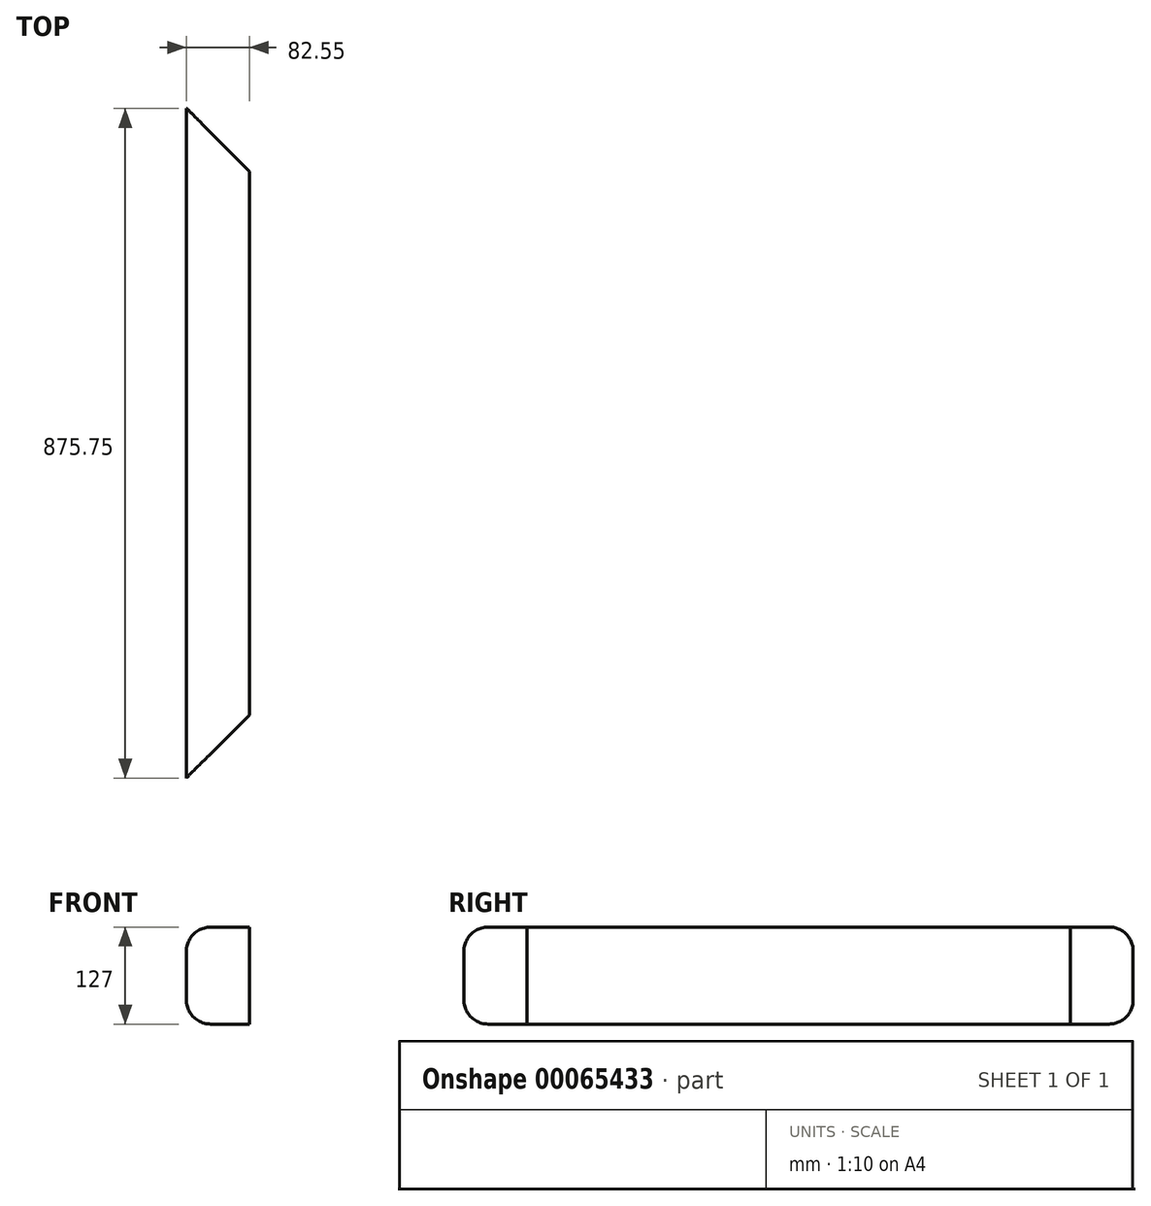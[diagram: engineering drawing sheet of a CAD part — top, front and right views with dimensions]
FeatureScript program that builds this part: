
annotation { "Feature Type Name" : "Feature", "Feature Type Description" : "" }
export const myFeature = defineFeature(function(context is Context, id is Id, definition is map)
    precondition{}
    {
        {
            var Q0;
            Q0=qCreatedBy(makeId("Front.planeOp"),FACE);
            var sketch = newSketch(context, id + "F0", { "sketchPlane" : qUnion([Q0])});
            skLineSegment(sketch, "E0.bottom", {"start": v(0, 0) * mm, "end": v(-50.8, 0) * mm});
            skLineSegment(sketch, "E0.top", {"start": v(0, -127) * mm, "end": v(-50.8, -127) * mm});
            skLineSegment(sketch, "E0.left", {"start": v(0, 0) * mm, "end": v(0, -127) * mm});
            skLineSegment(sketch, "E0.right", {"start": v(-82.55, -31.75) * mm, "end": v(-82.55, -95.25) * mm});
            skPoint(sketch, "E1.visualSharp", {"position": v(-82.55, 0) * mm});
            skArc(sketch, "E1.filletArc", {"start": v(-50.8, 0) * mm, "mid": v(-73.25, -9.3) * mm, "end": v(-82.55, -31.75) * mm});
            skPoint(sketch, "E2.visualSharp", {"position": v(-82.55, -127) * mm});
            skArc(sketch, "E2.filletArc", {"start": v(-82.55, -95.25) * mm, "mid": v(-73.25, -117.7) * mm, "end": v(-50.8, -127) * mm});
            skSolve(sketch);
        }
        {
            var Q0;
            Q0=qSketchRegion(id+"F0",true);
            extrude(context, id + "F1", {"entities" : qUnion([Q0]), "depth" : 1016 * mm});
        }
        {
            var Q0;
            Q0=makeQuery(id+"F1.opExtrude","SWEPT_FACE",FACE,{"disambiguationData":[OSD([sQuery(id+"F0.wireOp",EDGE,"E0.bottom")])]});
            var sketch = newSketch(context, id + "F2", { "sketchPlane" : qUnion([Q0])});
            skLineSegment(sketch, "E3", {"start": v(0, 0) * mm, "end": v(-82, 0) * mm});
            skLineSegment(sketch, "E4", {"start": v(-82, 0) * mm, "end": v(0, -82) * mm});
            skLineSegment(sketch, "E5", {"start": v(0, -82) * mm, "end": v(0, 0) * mm});
            skSolve(sketch);
        }
        {
            var Q0;
            Q0=qSketchRegion(id+"F2",true);
            extrude(context, id + "F3", {"entities" : qUnion([Q0]), "operationType" : NewBodyOperationType.REMOVE, "endBound" : BoundingType.THROUGH_ALL, "oppositeDirection" : true, "depth" : 25.4 * mm});
        }
        {
            var Q0;
            Q0=makeQuery(id+"F1.opExtrude","SWEPT_FACE",FACE,{"disambiguationData":[OSD([sQuery(id+"F0.wireOp",EDGE,"E0.bottom")])]});
            var sketch = newSketch(context, id + "F4", { "sketchPlane" : qUnion([Q0])});
            skLineSegment(sketch, "E6", {"start": v(0, -793.2) * mm, "end": v(-222.8, -1016) * mm});
            skLineSegment(sketch, "E7", {"start": v(0, -793.2) * mm, "end": v(0, -1016) * mm});
            skLineSegment(sketch, "E8", {"start": v(0, -1016) * mm, "end": v(-222.8, -1016) * mm});
            skSolve(sketch);
        }
        {
            var Q0;
            Q0=qSketchRegion(id+"F4",true);
            extrude(context, id + "F5", {"entities" : qUnion([Q0]), "operationType" : NewBodyOperationType.REMOVE, "endBound" : BoundingType.THROUGH_ALL, "oppositeDirection" : true, "depth" : 25.4 * mm});
        }
    });
